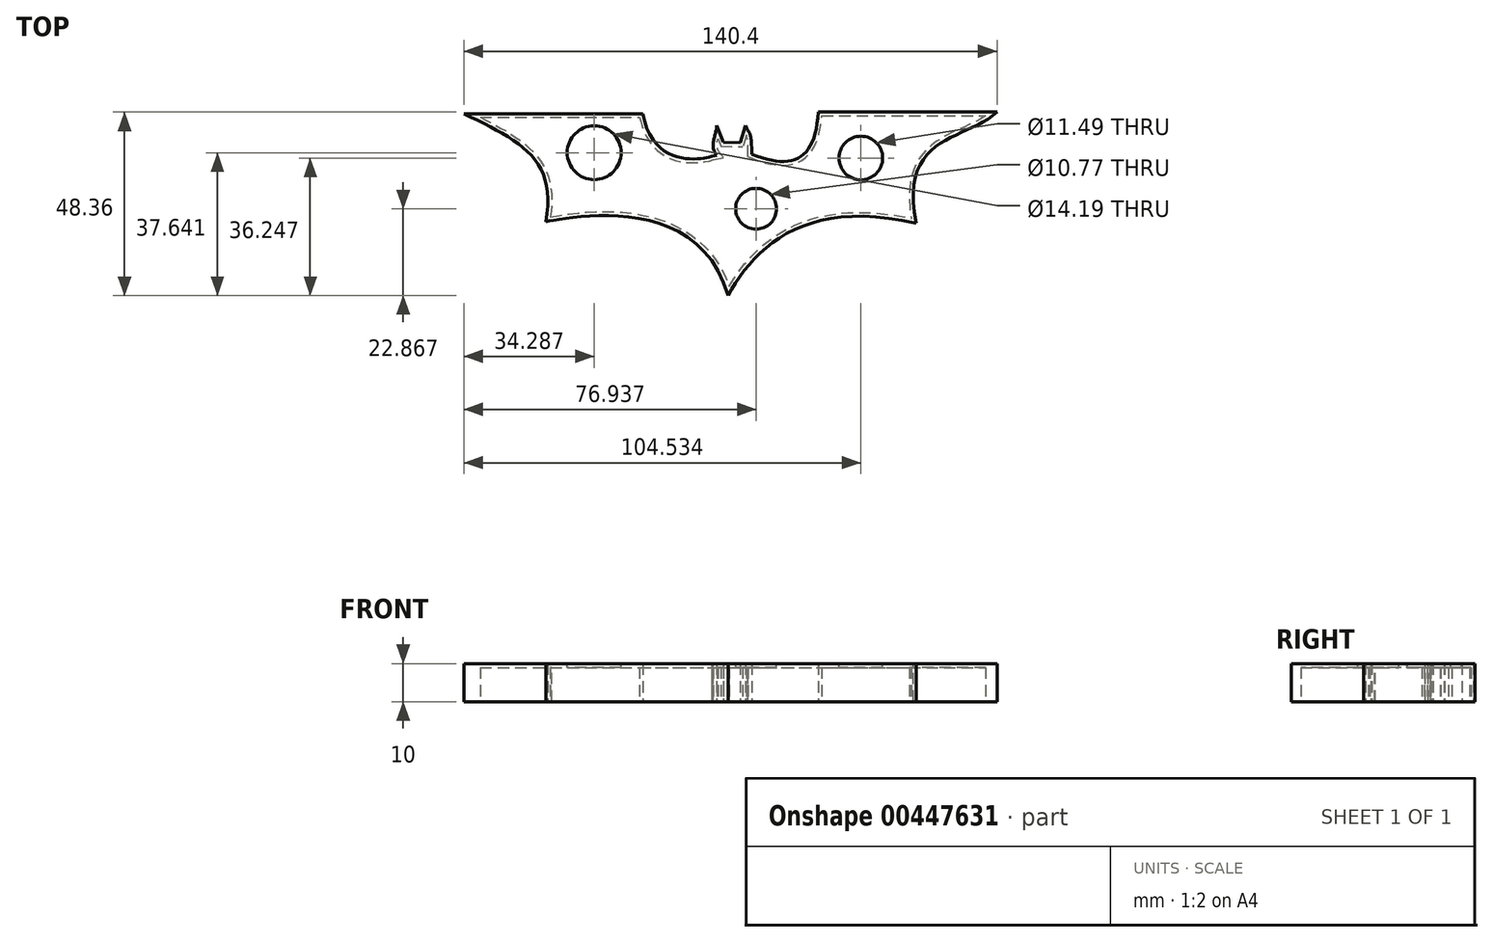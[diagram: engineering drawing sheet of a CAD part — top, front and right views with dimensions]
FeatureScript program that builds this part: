
annotation { "Feature Type Name" : "Feature", "Feature Type Description" : "" }
export const myFeature = defineFeature(function(context is Context, id is Id, definition is map)
    precondition{}
    {
        {
            var Q0;
            Q0=qCreatedBy(makeId("Top.planeOp"),FACE);
            var sketch = newSketch(context, id + "F0", { "sketchPlane" : qUnion([Q0])});
            skLineSegment(sketch, "E0", {"start": v(-69.55, 19.08) * mm, "end": v(-22.45, 19.08) * mm});
            skLineSegment(sketch, "E1", {"start": v(23.75, 19.5) * mm, "end": v(70.85, 19.5) * mm});
            skFitSpline(sketch, "E2", {"points": [v(-69.55, 19.08) * mm, v(-48, -9.4) * mm], "startDerivative": vector(41.82, -20.64) * mm, "endDerivative": vector(-9.65, -50.83) * mm});
            skFitSpline(sketch, "E3", {"points": [v(-48, -9.4) * mm, v(0, -28.86) * mm], "startDerivative": vector(16.72, 3.08) * mm, "endDerivative": vector(23.82, -83.75) * mm});
            skFitSpline(sketch, "E4", {"points": [v(-22.45, 19.08) * mm, v(-4.29, 7.85) * mm], "startDerivative": vector(8.9, -49.9) * mm, "endDerivative": vector(-3.95, -0.88) * mm});
            skFitSpline(sketch, "E5", {"points": [v(-2.97, 8.14) * mm, v(-2.97, 16.03) * mm], "startDerivative": vector(-6.58, 8.33) * mm, "endDerivative": vector(0, 7.9) * mm});
            skFitSpline(sketch, "E6", {"points": [v(6.22, 8.42) * mm, v(4.63, 16.03) * mm], "startDerivative": vector(0, 22.36) * mm, "endDerivative": vector(-1.9, 8.04) * mm});
            skFitSpline(sketch, "E7", {"points": [v(-2.97, 16.03) * mm, v(-1.22, 11.5) * mm], "startDerivative": vector(1.75, -4.53) * mm, "endDerivative": vector(1.75, -4.53) * mm});
            skFitSpline(sketch, "E8", {"points": [v(4.63, 16.03) * mm, v(3.17, 11.36) * mm], "startDerivative": vector(-1.46, -4.68) * mm, "endDerivative": vector(-2.92, -9.35) * mm});
            skFitSpline(sketch, "E9", {"points": [v(70.85, 19.5) * mm, v(49.5, -9.84) * mm], "startDerivative": vector(-25.55, -23.31) * mm, "endDerivative": vector(13.6, -71.03) * mm});
            skFitSpline(sketch, "E10", {"points": [v(0, -28.86) * mm, v(49.5, -9.84) * mm], "startDerivative": vector(20.9, 38.2) * mm, "endDerivative": vector(87.26, -20.6) * mm});
            skFitSpline(sketch, "E11", {"points": [v(6.22, 8.42) * mm, v(23.75, 19.5) * mm], "startDerivative": vector(32.26, -13.37) * mm, "endDerivative": vector(1.78, 37.73) * mm});
            skLineSegment(sketch, "E12", {"start": v(-4.29, 7.85) * mm, "end": v(-2.97, 8.14) * mm});
            skLineSegment(sketch, "E13", {"start": v(-1.22, 11.5) * mm, "end": v(3.17, 11.36) * mm});
            skSolve(sketch);
        }
        {
            var Q0;
            Q0=makeQuery(id+"F0.imprint","IMPRINT",FACE,{"disambiguationData":[TD([[makeQuery(id+"F0.imprint","IMPRINT",EDGE,{"derivedFrom":sQuery(id+"F0.wireOp",EDGE,"E0")}),-1.0]])]});
            extrude(context, id + "F1", {"entities" : qUnion([Q0]), "depth" : 10 * mm});
        }
        {
            var Q0;
            Q0=makeQuery(id+"F1.opExtrude","CAP_FACE",FACE,{"disambiguationData":[OSD([sQuery(id+"F0.wireOp",EDGE,"E0"),sQuery(id+"F0.wireOp",EDGE,"E1"),sQuery(id+"F0.wireOp",EDGE,"E2"),sQuery(id+"F0.wireOp",EDGE,"E3"),sQuery(id+"F0.wireOp",EDGE,"E4"),sQuery(id+"F0.wireOp",EDGE,"E5"),sQuery(id+"F0.wireOp",EDGE,"E6"),sQuery(id+"F0.wireOp",EDGE,"E7"),sQuery(id+"F0.wireOp",EDGE,"E8"),sQuery(id+"F0.wireOp",EDGE,"E9"),sQuery(id+"F0.wireOp",EDGE,"E10"),sQuery(id+"F0.wireOp",EDGE,"E11"),sQuery(id+"F0.wireOp",EDGE,"E12"),sQuery(id+"F0.wireOp",EDGE,"E13")])],"isStart":true});
            shell(context, id + "F2", {"entities" : qUnion([Q0]), "thickness" : 1 * mm});
        }
        {
            var Q0;
            Q0=makeQuery(id+"F1.opExtrude","CAP_FACE",FACE,{"disambiguationData":[OSD([sQuery(id+"F0.wireOp",EDGE,"E0"),sQuery(id+"F0.wireOp",EDGE,"E1"),sQuery(id+"F0.wireOp",EDGE,"E2"),sQuery(id+"F0.wireOp",EDGE,"E3"),sQuery(id+"F0.wireOp",EDGE,"E4"),sQuery(id+"F0.wireOp",EDGE,"E5"),sQuery(id+"F0.wireOp",EDGE,"E6"),sQuery(id+"F0.wireOp",EDGE,"E7"),sQuery(id+"F0.wireOp",EDGE,"E8"),sQuery(id+"F0.wireOp",EDGE,"E9"),sQuery(id+"F0.wireOp",EDGE,"E10"),sQuery(id+"F0.wireOp",EDGE,"E11"),sQuery(id+"F0.wireOp",EDGE,"E12"),sQuery(id+"F0.wireOp",EDGE,"E13")])],"isStart":false});
            var sketch = newSketch(context, id + "F3", { "sketchPlane" : qUnion([Q0])});
            skCircle(sketch, "E14", {"center": v(-35.26, 8.78) * mm, "radius": 7.1 * mm});
            skCircle(sketch, "E15", {"center": v(7.39, -6) * mm, "radius": 5.38 * mm});
            skCircle(sketch, "E16", {"center": v(34.98, 7.39) * mm, "radius": 5.75 * mm});
            skSolve(sketch);
        }
        {
            var Q0;
            Q0 = qSketchRegion(id + "F3", true);
            extrude(context, id + "F4", {"entities" : qUnion([Q0]), "operationType" : NewBodyOperationType.REMOVE, "oppositeDirection" : true, "depth" : 25 * mm});
        }
    });
